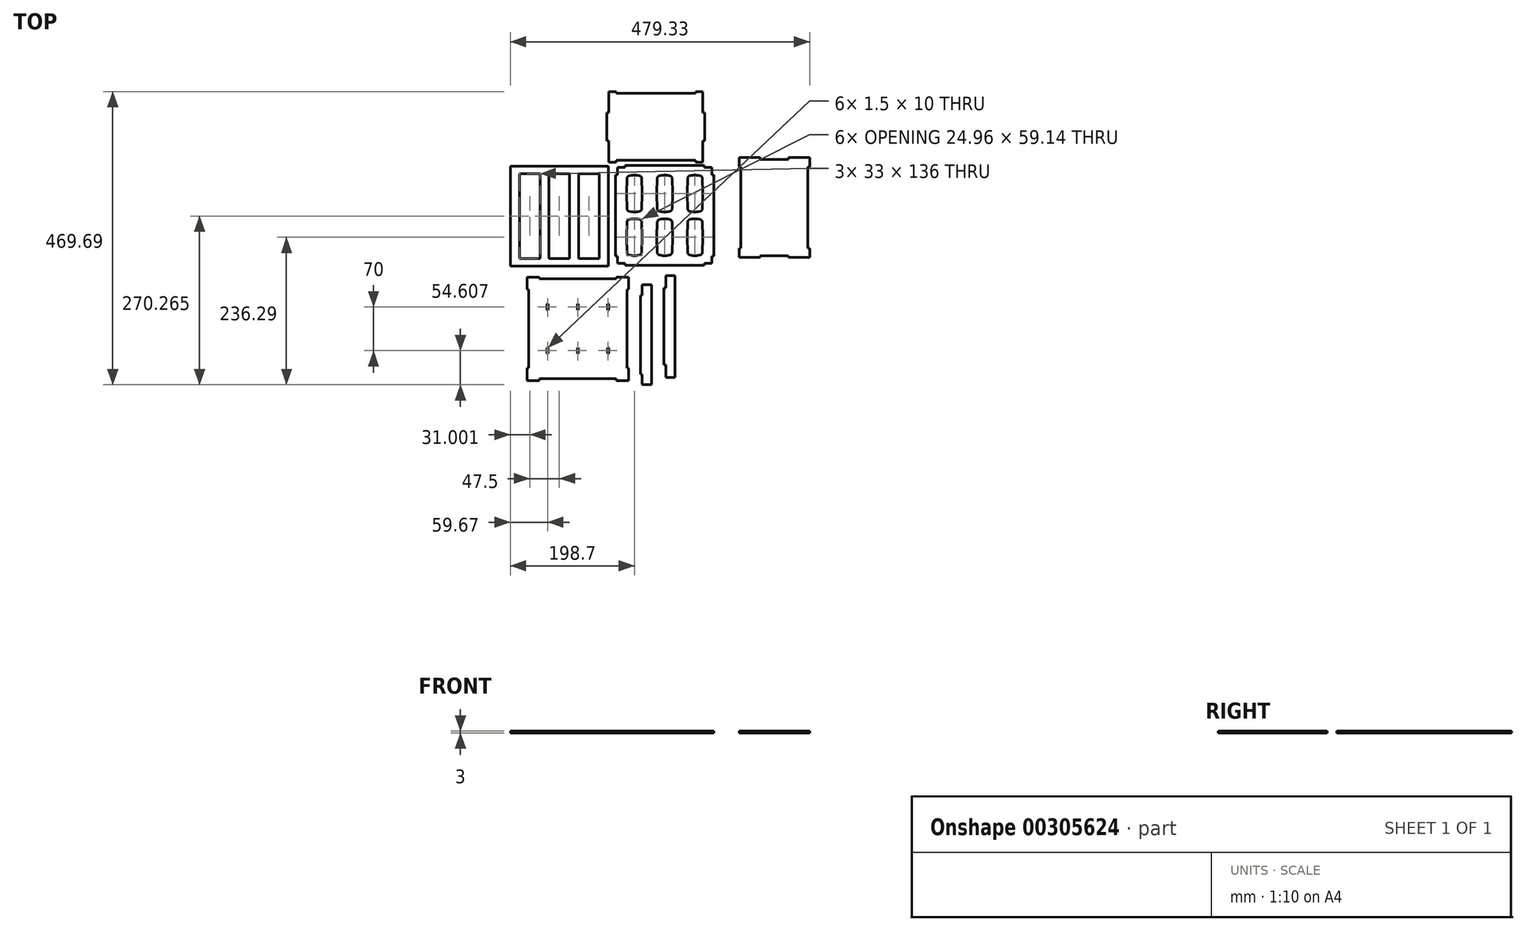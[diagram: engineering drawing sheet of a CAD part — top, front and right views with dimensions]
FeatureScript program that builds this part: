
annotation { "Feature Type Name" : "Feature", "Feature Type Description" : "" }
export const myFeature = defineFeature(function(context is Context, id is Id, definition is map)
    precondition{}
    {
        {
            var Q0;
            Q0=qCreatedBy(makeId("Top.planeOp"),FACE);
            var sketch = newSketch(context, id + "F0", { "sketchPlane" : qUnion([Q0])});
            skLineSegment(sketch, "E0.bottom", {"start": v(12.5, -30) * mm, "end": v(-12.5, -30) * mm, "construction": true});
            skLineSegment(sketch, "E0.top", {"start": v(12.5, 30) * mm, "end": v(-12.5, 30) * mm, "construction": true});
            skLineSegment(sketch, "E0.left", {"start": v(12.5, -30) * mm, "end": v(12.5, 30) * mm, "construction": true});
            skLineSegment(sketch, "E0.right", {"start": v(-12.5, -30) * mm, "end": v(-12.5, 30) * mm, "construction": true});
            skPoint(sketch, "E0.middle", {"position": v(0, 0) * mm});
            skLineSegment(sketch, "E1", {"start": v(-5.03, 29.14) * mm, "end": v(-7.7, 28.69) * mm});
            skLineSegment(sketch, "E2", {"start": v(-11.86, 23.9) * mm, "end": v(-12.46, 1.34) * mm});
            skLineSegment(sketch, "E3", {"start": v(5.03, 29.14) * mm, "end": v(7.7, 28.69) * mm});
            skLineSegment(sketch, "E4", {"start": v(11.86, 23.9) * mm, "end": v(12.46, 1.34) * mm});
            skLineSegment(sketch, "E5", {"start": v(12.46, -1.34) * mm, "end": v(11.86, -23.9) * mm});
            skLineSegment(sketch, "E6", {"start": v(7.7, -28.69) * mm, "end": v(5.03, -29.14) * mm});
            skLineSegment(sketch, "E7", {"start": v(-5.03, -29.14) * mm, "end": v(-7.7, -28.69) * mm});
            skLineSegment(sketch, "E8", {"start": v(-11.86, -23.9) * mm, "end": v(-12.46, -1.34) * mm});
            skPoint(sketch, "E9.visualSharp", {"position": v(-11.75, 28) * mm});
            skArc(sketch, "E9.filletArc", {"start": v(-7.7, 28.69) * mm, "mid": v(-10.64, 27.04) * mm, "end": v(-11.86, 23.9) * mm});
            skPoint(sketch, "E10.visualSharp", {"position": v(11.75, 28) * mm});
            skArc(sketch, "E10.filletArc", {"start": v(11.86, 23.9) * mm, "mid": v(10.64, 27.04) * mm, "end": v(7.7, 28.69) * mm});
            skPoint(sketch, "E11.visualSharp", {"position": v(11.75, -28) * mm});
            skArc(sketch, "E11.filletArc", {"start": v(7.7, -28.69) * mm, "mid": v(10.64, -27.04) * mm, "end": v(11.86, -23.9) * mm});
            skPoint(sketch, "E12.visualSharp", {"position": v(-11.75, -28) * mm});
            skArc(sketch, "E12.filletArc", {"start": v(-11.86, -23.9) * mm, "mid": v(-10.64, -27.04) * mm, "end": v(-7.7, -28.69) * mm});
            skPoint(sketch, "E13.visualSharp", {"position": v(0, -30) * mm});
            skArc(sketch, "E13.filletArc", {"start": v(-5.03, -29.14) * mm, "mid": v(0, -29.57) * mm, "end": v(5.03, -29.14) * mm});
            skPoint(sketch, "E14.visualSharp", {"position": v(0, 30) * mm});
            skArc(sketch, "E14.filletArc", {"start": v(5.03, 29.14) * mm, "mid": v(0, 29.57) * mm, "end": v(-5.03, 29.14) * mm});
            skPoint(sketch, "E15.visualSharp", {"position": v(-12.5, 0) * mm});
            skArc(sketch, "E15.filletArc", {"start": v(-12.46, 1.34) * mm, "mid": v(-12.48, 0) * mm, "end": v(-12.46, -1.34) * mm});
            skPoint(sketch, "E16.visualSharp", {"position": v(12.5, 0) * mm});
            skArc(sketch, "E16.filletArc", {"start": v(12.46, -1.34) * mm, "mid": v(12.48, 0) * mm, "end": v(12.46, 1.34) * mm});
            skPoint(sketch, "E17.0.1.0", {"position": v(0, 100) * mm});
            skLineSegment(sketch, "E17.0.1.1", {"start": v(12.46, 68.66) * mm, "end": v(11.86, 46.1) * mm});
            skLineSegment(sketch, "E17.0.1.2", {"start": v(11.86, 93.9) * mm, "end": v(12.46, 71.34) * mm});
            skLineSegment(sketch, "E17.0.1.3", {"start": v(-12.5, 40) * mm, "end": v(-12.5, 100) * mm, "construction": true});
            skLineSegment(sketch, "E17.0.1.4", {"start": v(12.5, 40) * mm, "end": v(12.5, 100) * mm, "construction": true});
            skPoint(sketch, "E17.0.1.5", {"position": v(-12.5, 70) * mm});
            skPoint(sketch, "E17.0.1.6", {"position": v(12.5, 70) * mm});
            skPoint(sketch, "E17.0.1.7", {"position": v(-11.75, 98) * mm});
            skPoint(sketch, "E17.0.1.8", {"position": v(11.75, 42) * mm});
            skPoint(sketch, "E17.0.1.9", {"position": v(-11.75, 42) * mm});
            skPoint(sketch, "E17.0.1.10", {"position": v(0, 40) * mm});
            skPoint(sketch, "E17.0.1.11", {"position": v(11.75, 98) * mm});
            skArc(sketch, "E17.0.1.12", {"start": v(5.03, 99.14) * mm, "mid": v(0, 99.57) * mm, "end": v(-5.03, 99.14) * mm});
            skArc(sketch, "E17.0.1.13", {"start": v(-5.03, 40.86) * mm, "mid": v(0, 40.43) * mm, "end": v(5.03, 40.86) * mm});
            skLineSegment(sketch, "E17.0.1.14", {"start": v(-11.86, 46.1) * mm, "end": v(-12.46, 68.66) * mm});
            skPoint(sketch, "E17.0.1.15", {"position": v(0, 70) * mm});
            skLineSegment(sketch, "E17.0.1.16", {"start": v(-11.86, 93.9) * mm, "end": v(-12.46, 71.34) * mm});
            skLineSegment(sketch, "E17.0.1.17", {"start": v(12.5, 100) * mm, "end": v(-12.5, 100) * mm, "construction": true});
            skLineSegment(sketch, "E17.0.1.18", {"start": v(12.5, 40) * mm, "end": v(-12.5, 40) * mm, "construction": true});
            skLineSegment(sketch, "E17.0.1.19", {"start": v(-5.03, 40.86) * mm, "end": v(-7.7, 41.31) * mm});
            skLineSegment(sketch, "E17.0.1.20", {"start": v(7.7, 41.31) * mm, "end": v(5.03, 40.86) * mm});
            skArc(sketch, "E17.0.1.21", {"start": v(-11.86, 46.1) * mm, "mid": v(-10.64, 42.96) * mm, "end": v(-7.7, 41.31) * mm});
            skArc(sketch, "E17.0.1.22", {"start": v(7.7, 41.31) * mm, "mid": v(10.64, 42.96) * mm, "end": v(11.86, 46.1) * mm});
            skArc(sketch, "E17.0.1.23", {"start": v(11.86, 93.9) * mm, "mid": v(10.64, 97.04) * mm, "end": v(7.7, 98.69) * mm});
            skArc(sketch, "E17.0.1.24", {"start": v(-7.7, 98.69) * mm, "mid": v(-10.64, 97.04) * mm, "end": v(-11.86, 93.9) * mm});
            skLineSegment(sketch, "E17.0.1.25", {"start": v(5.03, 99.14) * mm, "end": v(7.7, 98.69) * mm});
            skLineSegment(sketch, "E17.0.1.26", {"start": v(-5.03, 99.14) * mm, "end": v(-7.7, 98.69) * mm});
            skArc(sketch, "E17.0.1.27", {"start": v(-12.46, 71.34) * mm, "mid": v(-12.48, 70) * mm, "end": v(-12.46, 68.66) * mm});
            skArc(sketch, "E17.0.1.28", {"start": v(12.46, 68.66) * mm, "mid": v(12.48, 70) * mm, "end": v(12.46, 71.34) * mm});
            skPoint(sketch, "E17.1.0.0", {"position": v(48.5, 30) * mm});
            skLineSegment(sketch, "E17.1.0.1", {"start": v(60.96, -1.34) * mm, "end": v(60.36, -23.9) * mm});
            skLineSegment(sketch, "E17.1.0.2", {"start": v(60.36, 23.9) * mm, "end": v(60.96, 1.34) * mm});
            skLineSegment(sketch, "E17.1.0.3", {"start": v(36, -30) * mm, "end": v(36, 30) * mm, "construction": true});
            skLineSegment(sketch, "E17.1.0.4", {"start": v(61, -30) * mm, "end": v(61, 30) * mm, "construction": true});
            skPoint(sketch, "E17.1.0.5", {"position": v(36, 0) * mm});
            skPoint(sketch, "E17.1.0.6", {"position": v(61, 0) * mm});
            skPoint(sketch, "E17.1.0.7", {"position": v(36.75, 28) * mm});
            skPoint(sketch, "E17.1.0.8", {"position": v(60.25, -28) * mm});
            skPoint(sketch, "E17.1.0.9", {"position": v(36.75, -28) * mm});
            skPoint(sketch, "E17.1.0.10", {"position": v(48.5, -30) * mm});
            skPoint(sketch, "E17.1.0.11", {"position": v(60.25, 28) * mm});
            skArc(sketch, "E17.1.0.12", {"start": v(53.53, 29.14) * mm, "mid": v(48.5, 29.57) * mm, "end": v(43.47, 29.14) * mm});
            skArc(sketch, "E17.1.0.13", {"start": v(43.47, -29.14) * mm, "mid": v(48.5, -29.57) * mm, "end": v(53.53, -29.14) * mm});
            skLineSegment(sketch, "E17.1.0.14", {"start": v(36.64, -23.9) * mm, "end": v(36.04, -1.34) * mm});
            skPoint(sketch, "E17.1.0.15", {"position": v(48.5, 0) * mm});
            skLineSegment(sketch, "E17.1.0.16", {"start": v(36.64, 23.9) * mm, "end": v(36.04, 1.34) * mm});
            skLineSegment(sketch, "E17.1.0.17", {"start": v(61, 30) * mm, "end": v(36, 30) * mm, "construction": true});
            skLineSegment(sketch, "E17.1.0.18", {"start": v(61, -30) * mm, "end": v(36, -30) * mm, "construction": true});
            skLineSegment(sketch, "E17.1.0.19", {"start": v(43.47, -29.14) * mm, "end": v(40.8, -28.69) * mm});
            skLineSegment(sketch, "E17.1.0.20", {"start": v(56.2, -28.69) * mm, "end": v(53.53, -29.14) * mm});
            skArc(sketch, "E17.1.0.21", {"start": v(36.64, -23.9) * mm, "mid": v(37.86, -27.04) * mm, "end": v(40.8, -28.69) * mm});
            skArc(sketch, "E17.1.0.22", {"start": v(56.2, -28.69) * mm, "mid": v(59.14, -27.04) * mm, "end": v(60.36, -23.9) * mm});
            skArc(sketch, "E17.1.0.23", {"start": v(60.36, 23.9) * mm, "mid": v(59.14, 27.04) * mm, "end": v(56.2, 28.69) * mm});
            skArc(sketch, "E17.1.0.24", {"start": v(40.8, 28.69) * mm, "mid": v(37.86, 27.04) * mm, "end": v(36.64, 23.9) * mm});
            skLineSegment(sketch, "E17.1.0.25", {"start": v(53.53, 29.14) * mm, "end": v(56.2, 28.69) * mm});
            skLineSegment(sketch, "E17.1.0.26", {"start": v(43.47, 29.14) * mm, "end": v(40.8, 28.69) * mm});
            skArc(sketch, "E17.1.0.27", {"start": v(36.04, 1.34) * mm, "mid": v(36.02, 0) * mm, "end": v(36.04, -1.34) * mm});
            skArc(sketch, "E17.1.0.28", {"start": v(60.96, -1.34) * mm, "mid": v(60.98, 0) * mm, "end": v(60.96, 1.34) * mm});
            skPoint(sketch, "E17.1.1.0", {"position": v(48.5, 100) * mm});
            skLineSegment(sketch, "E17.1.1.1", {"start": v(60.96, 68.66) * mm, "end": v(60.36, 46.1) * mm});
            skLineSegment(sketch, "E17.1.1.2", {"start": v(60.36, 93.9) * mm, "end": v(60.96, 71.34) * mm});
            skLineSegment(sketch, "E17.1.1.3", {"start": v(36, 40) * mm, "end": v(36, 100) * mm, "construction": true});
            skLineSegment(sketch, "E17.1.1.4", {"start": v(61, 40) * mm, "end": v(61, 100) * mm, "construction": true});
            skPoint(sketch, "E17.1.1.5", {"position": v(36, 70) * mm});
            skPoint(sketch, "E17.1.1.6", {"position": v(61, 70) * mm});
            skPoint(sketch, "E17.1.1.7", {"position": v(36.75, 98) * mm});
            skPoint(sketch, "E17.1.1.8", {"position": v(60.25, 42) * mm});
            skPoint(sketch, "E17.1.1.9", {"position": v(36.75, 42) * mm});
            skPoint(sketch, "E17.1.1.10", {"position": v(48.5, 40) * mm});
            skPoint(sketch, "E17.1.1.11", {"position": v(60.25, 98) * mm});
            skArc(sketch, "E17.1.1.12", {"start": v(53.53, 99.14) * mm, "mid": v(48.5, 99.57) * mm, "end": v(43.47, 99.14) * mm});
            skArc(sketch, "E17.1.1.13", {"start": v(43.47, 40.86) * mm, "mid": v(48.5, 40.43) * mm, "end": v(53.53, 40.86) * mm});
            skLineSegment(sketch, "E17.1.1.14", {"start": v(36.64, 46.1) * mm, "end": v(36.04, 68.66) * mm});
            skPoint(sketch, "E17.1.1.15", {"position": v(48.5, 70) * mm});
            skLineSegment(sketch, "E17.1.1.16", {"start": v(36.64, 93.9) * mm, "end": v(36.04, 71.34) * mm});
            skLineSegment(sketch, "E17.1.1.17", {"start": v(61, 100) * mm, "end": v(36, 100) * mm, "construction": true});
            skLineSegment(sketch, "E17.1.1.18", {"start": v(61, 40) * mm, "end": v(36, 40) * mm, "construction": true});
            skLineSegment(sketch, "E17.1.1.19", {"start": v(43.47, 40.86) * mm, "end": v(40.8, 41.31) * mm});
            skLineSegment(sketch, "E17.1.1.20", {"start": v(56.2, 41.31) * mm, "end": v(53.53, 40.86) * mm});
            skArc(sketch, "E17.1.1.21", {"start": v(36.64, 46.1) * mm, "mid": v(37.86, 42.96) * mm, "end": v(40.8, 41.31) * mm});
            skArc(sketch, "E17.1.1.22", {"start": v(56.2, 41.31) * mm, "mid": v(59.14, 42.96) * mm, "end": v(60.36, 46.1) * mm});
            skArc(sketch, "E17.1.1.23", {"start": v(60.36, 93.9) * mm, "mid": v(59.14, 97.04) * mm, "end": v(56.2, 98.69) * mm});
            skArc(sketch, "E17.1.1.24", {"start": v(40.8, 98.69) * mm, "mid": v(37.86, 97.04) * mm, "end": v(36.64, 93.9) * mm});
            skLineSegment(sketch, "E17.1.1.25", {"start": v(53.53, 99.14) * mm, "end": v(56.2, 98.69) * mm});
            skLineSegment(sketch, "E17.1.1.26", {"start": v(43.47, 99.14) * mm, "end": v(40.8, 98.69) * mm});
            skArc(sketch, "E17.1.1.27", {"start": v(36.04, 71.34) * mm, "mid": v(36.02, 70) * mm, "end": v(36.04, 68.66) * mm});
            skArc(sketch, "E17.1.1.28", {"start": v(60.96, 68.66) * mm, "mid": v(60.98, 70) * mm, "end": v(60.96, 71.34) * mm});
            skPoint(sketch, "E17.2.0.0", {"position": v(97, 30) * mm});
            skLineSegment(sketch, "E17.2.0.1", {"start": v(109.46, -1.34) * mm, "end": v(108.86, -23.9) * mm});
            skLineSegment(sketch, "E17.2.0.2", {"start": v(108.86, 23.9) * mm, "end": v(109.46, 1.34) * mm});
            skLineSegment(sketch, "E17.2.0.3", {"start": v(84.5, -30) * mm, "end": v(84.5, 30) * mm, "construction": true});
            skLineSegment(sketch, "E17.2.0.4", {"start": v(109.5, -30) * mm, "end": v(109.5, 30) * mm, "construction": true});
            skPoint(sketch, "E17.2.0.5", {"position": v(84.5, 0) * mm});
            skPoint(sketch, "E17.2.0.6", {"position": v(109.5, 0) * mm});
            skPoint(sketch, "E17.2.0.7", {"position": v(85.25, 28) * mm});
            skPoint(sketch, "E17.2.0.8", {"position": v(108.75, -28) * mm});
            skPoint(sketch, "E17.2.0.9", {"position": v(85.25, -28) * mm});
            skPoint(sketch, "E17.2.0.10", {"position": v(97, -30) * mm});
            skPoint(sketch, "E17.2.0.11", {"position": v(108.75, 28) * mm});
            skArc(sketch, "E17.2.0.12", {"start": v(102.03, 29.14) * mm, "mid": v(97, 29.57) * mm, "end": v(91.97, 29.14) * mm});
            skArc(sketch, "E17.2.0.13", {"start": v(91.97, -29.14) * mm, "mid": v(97, -29.57) * mm, "end": v(102.03, -29.14) * mm});
            skLineSegment(sketch, "E17.2.0.14", {"start": v(85.14, -23.9) * mm, "end": v(84.54, -1.34) * mm});
            skPoint(sketch, "E17.2.0.15", {"position": v(97, 0) * mm});
            skLineSegment(sketch, "E17.2.0.16", {"start": v(85.14, 23.9) * mm, "end": v(84.54, 1.34) * mm});
            skLineSegment(sketch, "E17.2.0.17", {"start": v(109.5, 30) * mm, "end": v(84.5, 30) * mm, "construction": true});
            skLineSegment(sketch, "E17.2.0.18", {"start": v(109.5, -30) * mm, "end": v(84.5, -30) * mm, "construction": true});
            skLineSegment(sketch, "E17.2.0.19", {"start": v(91.97, -29.14) * mm, "end": v(89.3, -28.69) * mm});
            skLineSegment(sketch, "E17.2.0.20", {"start": v(104.7, -28.69) * mm, "end": v(102.03, -29.14) * mm});
            skArc(sketch, "E17.2.0.21", {"start": v(85.14, -23.9) * mm, "mid": v(86.36, -27.04) * mm, "end": v(89.3, -28.69) * mm});
            skArc(sketch, "E17.2.0.22", {"start": v(104.7, -28.69) * mm, "mid": v(107.64, -27.04) * mm, "end": v(108.86, -23.9) * mm});
            skArc(sketch, "E17.2.0.23", {"start": v(108.86, 23.9) * mm, "mid": v(107.64, 27.04) * mm, "end": v(104.7, 28.69) * mm});
            skArc(sketch, "E17.2.0.24", {"start": v(89.3, 28.69) * mm, "mid": v(86.36, 27.04) * mm, "end": v(85.14, 23.9) * mm});
            skLineSegment(sketch, "E17.2.0.25", {"start": v(102.03, 29.14) * mm, "end": v(104.7, 28.69) * mm});
            skLineSegment(sketch, "E17.2.0.26", {"start": v(91.97, 29.14) * mm, "end": v(89.3, 28.69) * mm});
            skArc(sketch, "E17.2.0.27", {"start": v(84.54, 1.34) * mm, "mid": v(84.52, 0) * mm, "end": v(84.54, -1.34) * mm});
            skArc(sketch, "E17.2.0.28", {"start": v(109.46, -1.34) * mm, "mid": v(109.48, 0) * mm, "end": v(109.46, 1.34) * mm});
            skPoint(sketch, "E17.2.1.0", {"position": v(97, 100) * mm});
            skLineSegment(sketch, "E17.2.1.1", {"start": v(109.46, 68.66) * mm, "end": v(108.86, 46.1) * mm});
            skLineSegment(sketch, "E17.2.1.2", {"start": v(108.86, 93.9) * mm, "end": v(109.46, 71.34) * mm});
            skLineSegment(sketch, "E17.2.1.3", {"start": v(84.5, 40) * mm, "end": v(84.5, 100) * mm, "construction": true});
            skLineSegment(sketch, "E17.2.1.4", {"start": v(109.5, 40) * mm, "end": v(109.5, 100) * mm, "construction": true});
            skPoint(sketch, "E17.2.1.5", {"position": v(84.5, 70) * mm});
            skPoint(sketch, "E17.2.1.6", {"position": v(109.5, 70) * mm});
            skPoint(sketch, "E17.2.1.7", {"position": v(85.25, 98) * mm});
            skPoint(sketch, "E17.2.1.8", {"position": v(108.75, 42) * mm});
            skPoint(sketch, "E17.2.1.9", {"position": v(85.25, 42) * mm});
            skPoint(sketch, "E17.2.1.10", {"position": v(97, 40) * mm});
            skPoint(sketch, "E17.2.1.11", {"position": v(108.75, 98) * mm});
            skArc(sketch, "E17.2.1.12", {"start": v(102.03, 99.14) * mm, "mid": v(97, 99.57) * mm, "end": v(91.97, 99.14) * mm});
            skArc(sketch, "E17.2.1.13", {"start": v(91.97, 40.86) * mm, "mid": v(97, 40.43) * mm, "end": v(102.03, 40.86) * mm});
            skLineSegment(sketch, "E17.2.1.14", {"start": v(85.14, 46.1) * mm, "end": v(84.54, 68.66) * mm});
            skPoint(sketch, "E17.2.1.15", {"position": v(97, 70) * mm});
            skLineSegment(sketch, "E17.2.1.16", {"start": v(85.14, 93.9) * mm, "end": v(84.54, 71.34) * mm});
            skLineSegment(sketch, "E17.2.1.17", {"start": v(109.5, 100) * mm, "end": v(84.5, 100) * mm, "construction": true});
            skLineSegment(sketch, "E17.2.1.18", {"start": v(109.5, 40) * mm, "end": v(84.5, 40) * mm, "construction": true});
            skLineSegment(sketch, "E17.2.1.19", {"start": v(91.97, 40.86) * mm, "end": v(89.3, 41.31) * mm});
            skLineSegment(sketch, "E17.2.1.20", {"start": v(104.7, 41.31) * mm, "end": v(102.03, 40.86) * mm});
            skArc(sketch, "E17.2.1.21", {"start": v(85.14, 46.1) * mm, "mid": v(86.36, 42.96) * mm, "end": v(89.3, 41.31) * mm});
            skArc(sketch, "E17.2.1.22", {"start": v(104.7, 41.31) * mm, "mid": v(107.64, 42.96) * mm, "end": v(108.86, 46.1) * mm});
            skArc(sketch, "E17.2.1.23", {"start": v(108.86, 93.9) * mm, "mid": v(107.64, 97.04) * mm, "end": v(104.7, 98.69) * mm});
            skArc(sketch, "E17.2.1.24", {"start": v(89.3, 98.69) * mm, "mid": v(86.36, 97.04) * mm, "end": v(85.14, 93.9) * mm});
            skLineSegment(sketch, "E17.2.1.25", {"start": v(102.03, 99.14) * mm, "end": v(104.7, 98.69) * mm});
            skLineSegment(sketch, "E17.2.1.26", {"start": v(91.97, 99.14) * mm, "end": v(89.3, 98.69) * mm});
            skArc(sketch, "E17.2.1.27", {"start": v(84.54, 71.34) * mm, "mid": v(84.52, 70) * mm, "end": v(84.54, 68.66) * mm});
            skArc(sketch, "E17.2.1.28", {"start": v(109.46, 68.66) * mm, "mid": v(109.48, 70) * mm, "end": v(109.46, 71.34) * mm});
            skLineSegment(sketch, "E17.direction1", {"start": v(-12.5, -30) * mm, "end": v(36, -30) * mm, "construction": true});
            skLineSegment(sketch, "E17.direction2", {"start": v(-12.5, -30) * mm, "end": v(-12.5, 40) * mm, "construction": true});
            skPoint(sketch, "E18.visualSharp", {"position": v(-30, 115) * mm});
            skPoint(sketch, "E19.visualSharp", {"position": v(127, 115) * mm});
            skPoint(sketch, "E20.visualSharp", {"position": v(-30, -45) * mm});
            skLineSegment(sketch, "E21.bottom", {"start": v(-15, 115) * mm, "end": v(112, 115) * mm});
            skLineSegment(sketch, "E21.top", {"start": v(-15, -45) * mm, "end": v(112, -45) * mm});
            skLineSegment(sketch, "E21.left", {"start": v(-30, 100) * mm, "end": v(-30, -30) * mm});
            skLineSegment(sketch, "E22", {"start": v(-30, 100) * mm, "end": v(-27, 100) * mm});
            skLineSegment(sketch, "E23", {"start": v(-27, 100) * mm, "end": v(-27, 112) * mm});
            skLineSegment(sketch, "E24", {"start": v(-27, 112) * mm, "end": v(-15, 112) * mm});
            skLineSegment(sketch, "E25", {"start": v(-15, 112) * mm, "end": v(-15, 115) * mm});
            skLineSegment(sketch, "E26", {"start": v(-30, -30) * mm, "end": v(-27, -30) * mm});
            skLineSegment(sketch, "E27", {"start": v(-27, -30) * mm, "end": v(-27, -42) * mm});
            skLineSegment(sketch, "E28", {"start": v(-27, -42) * mm, "end": v(-15, -42) * mm});
            skLineSegment(sketch, "E29", {"start": v(-15, -42) * mm, "end": v(-15, -45) * mm});
            skLineSegment(sketch, "E30", {"start": v(127, -30) * mm, "end": v(124, -30) * mm});
            skLineSegment(sketch, "E31", {"start": v(124, -30) * mm, "end": v(124, -42) * mm});
            skLineSegment(sketch, "E32", {"start": v(124, -42) * mm, "end": v(112, -42) * mm});
            skLineSegment(sketch, "E33", {"start": v(112, -42) * mm, "end": v(112, -45) * mm});
            skLineSegment(sketch, "E34", {"start": v(112, 115) * mm, "end": v(112, 112) * mm});
            skLineSegment(sketch, "E35", {"start": v(112, 112) * mm, "end": v(124, 112) * mm});
            skLineSegment(sketch, "E36", {"start": v(124, 112) * mm, "end": v(124, 100) * mm});
            skLineSegment(sketch, "E37", {"start": v(124, 100) * mm, "end": v(127, 100) * mm});
            skLineSegment(sketch, "E38", {"start": v(127, 100) * mm, "end": v(127, -30) * mm});
            skSolve(sketch);
        }
        {
            var Q0;
            Q0 = qSketchRegion(id + "F0", true);
            extrude(context, id + "F1", {"entities" : qUnion([Q0]), "depth" : 3 * mm});
        }
        {
            var Q0;
            Q0=qCreatedBy(makeId("Top.planeOp"),FACE);
            var sketch = newSketch(context, id + "F2", { "sketchPlane" : qUnion([Q0])});
            skPoint(sketch, "E39.visualSharp", {"position": v(-41.7, 113.97) * mm});
            skPoint(sketch, "E40.visualSharp", {"position": v(-41.7, -46.03) * mm});
            skPoint(sketch, "E41.visualSharp", {"position": v(-198.7, -46.03) * mm});
            skPoint(sketch, "E42.visualSharp", {"position": v(-198.7, 113.97) * mm});
            skLineSegment(sketch, "E43.bottom", {"start": v(-184.2, 101.97) * mm, "end": v(-151.2, 101.97) * mm});
            skLineSegment(sketch, "E43.top", {"start": v(-184.2, -34.03) * mm, "end": v(-151.2, -34.03) * mm});
            skLineSegment(sketch, "E43.left", {"start": v(-184.2, 101.97) * mm, "end": v(-184.2, -34.03) * mm});
            skLineSegment(sketch, "E43.right", {"start": v(-151.2, 101.97) * mm, "end": v(-151.2, -34.03) * mm});
            skLineSegment(sketch, "E44.bottom", {"start": v(-136.7, 101.97) * mm, "end": v(-103.7, 101.97) * mm});
            skLineSegment(sketch, "E44.top", {"start": v(-136.7, -34.03) * mm, "end": v(-103.7, -34.03) * mm});
            skLineSegment(sketch, "E44.left", {"start": v(-136.7, 101.97) * mm, "end": v(-136.7, -34.03) * mm});
            skLineSegment(sketch, "E44.right", {"start": v(-103.7, 101.97) * mm, "end": v(-103.7, -34.03) * mm});
            skLineSegment(sketch, "E45.bottom", {"start": v(-89.2, 101.97) * mm, "end": v(-56.2, 101.97) * mm});
            skLineSegment(sketch, "E45.top", {"start": v(-89.2, -34.03) * mm, "end": v(-56.2, -34.03) * mm});
            skLineSegment(sketch, "E45.left", {"start": v(-89.2, 101.97) * mm, "end": v(-89.2, -34.03) * mm});
            skLineSegment(sketch, "E45.right", {"start": v(-56.2, 101.97) * mm, "end": v(-56.2, -34.03) * mm});
            skLineSegment(sketch, "E46.bottom", {"start": v(-198.7, 113.97) * mm, "end": v(-41.7, 113.97) * mm});
            skLineSegment(sketch, "E46.top", {"start": v(-198.7, -46.03) * mm, "end": v(-41.7, -46.03) * mm});
            skLineSegment(sketch, "E46.left", {"start": v(-198.7, 113.97) * mm, "end": v(-198.7, -46.03) * mm});
            skLineSegment(sketch, "E46.right", {"start": v(-41.7, 113.97) * mm, "end": v(-41.7, -46.03) * mm});
            skSolve(sketch);
        }
        {
            var Q0;
            Q0 = qSketchRegion(id + "F2", true);
            extrude(context, id + "F3", {"entities" : qUnion([Q0]), "depth" : 3 * mm});
        }
        {
            var Q0;
            Q0=qCreatedBy(makeId("Top.planeOp"),FACE);
            var sketch = newSketch(context, id + "F4", { "sketchPlane" : qUnion([Q0])});
            skPoint(sketch, "E47.visualSharp", {"position": v(-5.49, -66.68) * mm});
            skPoint(sketch, "E48.visualSharp", {"position": v(-12.03, -226.68) * mm});
            skPoint(sketch, "E49.visualSharp", {"position": v(-169.03, -226.68) * mm});
            skPoint(sketch, "E50.visualSharp", {"position": v(-169.03, -66.68) * mm});
            skLineSegment(sketch, "E51.bottom", {"start": v(-138.28, -116.68) * mm, "end": v(-139.78, -116.68) * mm});
            skLineSegment(sketch, "E51.top", {"start": v(-138.28, -106.68) * mm, "end": v(-139.78, -106.68) * mm});
            skLineSegment(sketch, "E51.left", {"start": v(-138.28, -116.68) * mm, "end": v(-138.28, -106.68) * mm});
            skLineSegment(sketch, "E51.right", {"start": v(-139.78, -116.68) * mm, "end": v(-139.78, -106.68) * mm});
            skPoint(sketch, "E51.middle", {"position": v(-139.03, -111.68) * mm});
            skLineSegment(sketch, "E52.0.1.0", {"start": v(-139.78, -186.68) * mm, "end": v(-139.78, -176.68) * mm});
            skLineSegment(sketch, "E52.0.1.1", {"start": v(-138.28, -186.68) * mm, "end": v(-138.28, -176.68) * mm});
            skPoint(sketch, "E52.0.1.2", {"position": v(-139.03, -181.68) * mm});
            skLineSegment(sketch, "E52.0.1.3", {"start": v(-138.28, -176.68) * mm, "end": v(-139.78, -176.68) * mm});
            skLineSegment(sketch, "E52.0.1.4", {"start": v(-138.28, -186.68) * mm, "end": v(-139.78, -186.68) * mm});
            skLineSegment(sketch, "E52.1.0.0", {"start": v(-91.28, -116.68) * mm, "end": v(-91.28, -106.68) * mm});
            skLineSegment(sketch, "E52.1.0.1", {"start": v(-89.78, -116.68) * mm, "end": v(-89.78, -106.68) * mm});
            skPoint(sketch, "E52.1.0.2", {"position": v(-90.53, -111.68) * mm});
            skLineSegment(sketch, "E52.1.0.3", {"start": v(-89.78, -106.68) * mm, "end": v(-91.28, -106.68) * mm});
            skLineSegment(sketch, "E52.1.0.4", {"start": v(-89.78, -116.68) * mm, "end": v(-91.28, -116.68) * mm});
            skLineSegment(sketch, "E52.1.1.0", {"start": v(-91.28, -186.68) * mm, "end": v(-91.28, -176.68) * mm});
            skLineSegment(sketch, "E52.1.1.1", {"start": v(-89.78, -186.68) * mm, "end": v(-89.78, -176.68) * mm});
            skPoint(sketch, "E52.1.1.2", {"position": v(-90.53, -181.68) * mm});
            skLineSegment(sketch, "E52.1.1.3", {"start": v(-89.78, -176.68) * mm, "end": v(-91.28, -176.68) * mm});
            skLineSegment(sketch, "E52.1.1.4", {"start": v(-89.78, -186.68) * mm, "end": v(-91.28, -186.68) * mm});
            skLineSegment(sketch, "E52.2.0.0", {"start": v(-42.78, -116.68) * mm, "end": v(-42.78, -106.68) * mm});
            skLineSegment(sketch, "E52.2.0.1", {"start": v(-41.28, -116.68) * mm, "end": v(-41.28, -106.68) * mm});
            skPoint(sketch, "E52.2.0.2", {"position": v(-42.03, -111.68) * mm});
            skLineSegment(sketch, "E52.2.0.3", {"start": v(-41.28, -106.68) * mm, "end": v(-42.78, -106.68) * mm});
            skLineSegment(sketch, "E52.2.0.4", {"start": v(-41.28, -116.68) * mm, "end": v(-42.78, -116.68) * mm});
            skLineSegment(sketch, "E52.2.1.0", {"start": v(-42.78, -186.68) * mm, "end": v(-42.78, -176.68) * mm});
            skLineSegment(sketch, "E52.2.1.1", {"start": v(-41.28, -186.68) * mm, "end": v(-41.28, -176.68) * mm});
            skPoint(sketch, "E52.2.1.2", {"position": v(-42.03, -181.68) * mm});
            skLineSegment(sketch, "E52.2.1.3", {"start": v(-41.28, -176.68) * mm, "end": v(-42.78, -176.68) * mm});
            skLineSegment(sketch, "E52.2.1.4", {"start": v(-41.28, -186.68) * mm, "end": v(-42.78, -186.68) * mm});
            skLineSegment(sketch, "E52.direction1", {"start": v(-139.03, -111.68) * mm, "end": v(-90.53, -111.68) * mm, "construction": true});
            skLineSegment(sketch, "E52.direction2", {"start": v(-139.03, -111.68) * mm, "end": v(-139.03, -181.68) * mm, "construction": true});
            skLineSegment(sketch, "E53.bottom", {"start": v(-152.03, -66.68) * mm, "end": v(-29.03, -66.68) * mm});
            skLineSegment(sketch, "E53.top", {"start": v(-152.03, -226.68) * mm, "end": v(-29.03, -226.68) * mm});
            skLineSegment(sketch, "E53.left", {"start": v(-169.03, -83.68) * mm, "end": v(-169.03, -209.68) * mm});
            skLineSegment(sketch, "E53.right", {"start": v(-12.03, -83.68) * mm, "end": v(-12.03, -209.68) * mm});
            skLineSegment(sketch, "E54", {"start": v(-169.03, -83.68) * mm, "end": v(-172.03, -83.68) * mm});
            skLineSegment(sketch, "E55", {"start": v(-172.03, -83.68) * mm, "end": v(-172.03, -63.68) * mm});
            skLineSegment(sketch, "E56", {"start": v(-172.03, -63.68) * mm, "end": v(-152.03, -63.68) * mm});
            skLineSegment(sketch, "E57", {"start": v(-152.03, -63.68) * mm, "end": v(-152.03, -66.68) * mm});
            skLineSegment(sketch, "E58", {"start": v(-169.03, -209.68) * mm, "end": v(-172.03, -209.68) * mm});
            skLineSegment(sketch, "E59", {"start": v(-172.03, -209.68) * mm, "end": v(-172.03, -229.68) * mm});
            skLineSegment(sketch, "E60", {"start": v(-172.03, -229.68) * mm, "end": v(-152.03, -229.68) * mm});
            skLineSegment(sketch, "E61", {"start": v(-152.03, -229.68) * mm, "end": v(-152.03, -226.68) * mm});
            skLineSegment(sketch, "E62", {"start": v(-29.03, -226.68) * mm, "end": v(-29.03, -229.68) * mm});
            skLineSegment(sketch, "E63", {"start": v(-29.03, -229.68) * mm, "end": v(-9.03, -229.68) * mm});
            skLineSegment(sketch, "E64", {"start": v(-9.03, -229.68) * mm, "end": v(-9.03, -209.68) * mm});
            skLineSegment(sketch, "E65", {"start": v(-9.03, -209.68) * mm, "end": v(-12.03, -209.68) * mm});
            skLineSegment(sketch, "E66", {"start": v(-12.03, -83.68) * mm, "end": v(-9.03, -83.68) * mm});
            skLineSegment(sketch, "E67", {"start": v(-9.03, -83.68) * mm, "end": v(-9.03, -63.68) * mm});
            skLineSegment(sketch, "E68", {"start": v(-9.03, -63.68) * mm, "end": v(-29.03, -63.68) * mm});
            skLineSegment(sketch, "E69", {"start": v(-29.03, -63.68) * mm, "end": v(-29.03, -66.68) * mm});
            skSolve(sketch);
        }
        {
            var Q0;
            Q0 = qSketchRegion(id + "F4", true);
            extrude(context, id + "F5", {"entities" : qUnion([Q0]), "depth" : 3 * mm});
        }
        {
            var Q0;
            Q0=qCreatedBy(makeId("Top.planeOp"),FACE);
            var sketch = newSketch(context, id + "F6", { "sketchPlane" : qUnion([Q0])});
            skLineSegment(sketch, "E70.bottom", {"start": v(12.59, -76.29) * mm, "end": v(27.59, -76.29) * mm});
            skLineSegment(sketch, "E70.top", {"start": v(12.59, -236.29) * mm, "end": v(27.59, -236.29) * mm});
            skLineSegment(sketch, "E70.left", {"start": v(9.59, -93.29) * mm, "end": v(9.59, -219.29) * mm});
            skLineSegment(sketch, "E70.right", {"start": v(27.59, -76.29) * mm, "end": v(27.59, -236.29) * mm});
            skLineSegment(sketch, "E71", {"start": v(9.59, -93.29) * mm, "end": v(12.59, -93.29) * mm});
            skLineSegment(sketch, "E72", {"start": v(12.59, -93.29) * mm, "end": v(12.59, -76.29) * mm});
            skLineSegment(sketch, "E73", {"start": v(9.59, -219.29) * mm, "end": v(12.59, -219.29) * mm});
            skLineSegment(sketch, "E74", {"start": v(12.59, -219.29) * mm, "end": v(12.59, -236.29) * mm});
            skSolve(sketch);
        }
        {
            var Q0;
            Q0 = qSketchRegion(id + "F6", true);
            extrude(context, id + "F7", {"entities" : qUnion([Q0]), "depth" : 3 * mm});
        }
        {
            var Q0;
            Q0=qCreatedBy(makeId("Top.planeOp"),FACE);
            var sketch = newSketch(context, id + "F8", { "sketchPlane" : qUnion([Q0])});
            skLineSegment(sketch, "E75.bottom", {"start": v(50.23, -61.3) * mm, "end": v(65.23, -61.3) * mm});
            skLineSegment(sketch, "E75.top", {"start": v(50.23, -224.3) * mm, "end": v(65.23, -224.3) * mm});
            skLineSegment(sketch, "E75.left", {"start": v(47.23, -81.3) * mm, "end": v(47.23, -204.3) * mm});
            skLineSegment(sketch, "E75.right", {"start": v(65.23, -61.3) * mm, "end": v(65.23, -224.3) * mm});
            skLineSegment(sketch, "E76", {"start": v(50.23, -61.3) * mm, "end": v(50.23, -81.3) * mm});
            skLineSegment(sketch, "E77", {"start": v(50.23, -81.3) * mm, "end": v(47.23, -81.3) * mm});
            skLineSegment(sketch, "E78", {"start": v(47.23, -204.3) * mm, "end": v(50.23, -204.3) * mm});
            skLineSegment(sketch, "E79", {"start": v(50.23, -204.3) * mm, "end": v(50.23, -224.3) * mm});
            skSolve(sketch);
        }
        {
            var Q0;
            Q0 = qSketchRegion(id + "F8", true);
            extrude(context, id + "F9", {"entities" : qUnion([Q0]), "depth" : 3 * mm});
        }
        {
            var Q0;
            Q0=qCreatedBy(makeId("Top.planeOp"),FACE);
            var sketch = newSketch(context, id + "F10", { "sketchPlane" : qUnion([Q0])});
            skLineSegment(sketch, "E80.bottom", {"start": v(170.6, 127.5) * mm, "end": v(201.63, 127.5) * mm});
            skLineSegment(sketch, "E80.top", {"start": v(170.6, -32.5) * mm, "end": v(201.63, -32.5) * mm});
            skLineSegment(sketch, "E81", {"start": v(167.63, 112.5) * mm, "end": v(170.63, 112.5) * mm});
            skLineSegment(sketch, "E82", {"start": v(201.63, 127.5) * mm, "end": v(201.63, 124.5) * mm});
            skLineSegment(sketch, "E83", {"start": v(201.63, 124.5) * mm, "end": v(246.63, 124.5) * mm});
            skLineSegment(sketch, "E84", {"start": v(246.63, 124.5) * mm, "end": v(246.63, 127.5) * mm});
            skLineSegment(sketch, "E85", {"start": v(277.63, 112.5) * mm, "end": v(280.63, 112.5) * mm});
            skLineSegment(sketch, "E86", {"start": v(167.63, -17.5) * mm, "end": v(170.63, -17.5) * mm});
            skLineSegment(sketch, "E87", {"start": v(201.63, -32.5) * mm, "end": v(201.63, -29.5) * mm});
            skLineSegment(sketch, "E88", {"start": v(201.63, -29.5) * mm, "end": v(246.63, -29.5) * mm});
            skLineSegment(sketch, "E89", {"start": v(246.63, -29.5) * mm, "end": v(246.63, -32.5) * mm});
            skLineSegment(sketch, "E90", {"start": v(277.63, -17.5) * mm, "end": v(280.63, -17.5) * mm});
            skLineSegment(sketch, "E91.trimOffspring", {"start": v(246.63, -32.5) * mm, "end": v(277.6, -32.5) * mm});
            skLineSegment(sketch, "E92.trimOffspring", {"start": v(246.63, 127.5) * mm, "end": v(277.6, 127.5) * mm});
            skLineSegment(sketch, "E93", {"start": v(170.63, 112.5) * mm, "end": v(170.63, -17.5) * mm});
            skLineSegment(sketch, "E94", {"start": v(277.63, 112.5) * mm, "end": v(277.63, -17.5) * mm});
            skLineSegment(sketch, "E95", {"start": v(167.63, -17.5) * mm, "end": v(167.63, -32.5) * mm});
            skLineSegment(sketch, "E96", {"start": v(167.63, -32.5) * mm, "end": v(170.6, -32.5) * mm});
            skLineSegment(sketch, "E97", {"start": v(280.63, -17.5) * mm, "end": v(280.63, -32.5) * mm});
            skLineSegment(sketch, "E98", {"start": v(280.63, -32.5) * mm, "end": v(277.6, -32.5) * mm});
            skLineSegment(sketch, "E99", {"start": v(280.63, 112.5) * mm, "end": v(280.63, 127.5) * mm});
            skLineSegment(sketch, "E100", {"start": v(280.63, 127.5) * mm, "end": v(277.6, 127.5) * mm});
            skLineSegment(sketch, "E101", {"start": v(167.63, 112.5) * mm, "end": v(167.63, 127.5) * mm});
            skLineSegment(sketch, "E102", {"start": v(167.63, 127.5) * mm, "end": v(170.6, 127.5) * mm});
            skSolve(sketch);
        }
        {
            var Q0;
            Q0 = qSketchRegion(id + "F10", true);
            extrude(context, id + "F11", {"entities" : qUnion([Q0]), "depth" : 3 * mm});
        }
        {
            var Q0;
            Q0=qCreatedBy(makeId("Top.planeOp"),FACE);
            var sketch = newSketch(context, id + "F12", { "sketchPlane" : qUnion([Q0])});
            skLineSegment(sketch, "E103.bottom", {"start": v(-41.26, 120.4) * mm, "end": v(-29.26, 120.4) * mm});
            skLineSegment(sketch, "E103.top", {"start": v(-41.26, 233.4) * mm, "end": v(-29.26, 233.4) * mm});
            skLineSegment(sketch, "E103.left", {"start": v(-44.26, 154.4) * mm, "end": v(-44.26, 199.4) * mm});
            skLineSegment(sketch, "E103.right", {"start": v(112.74, 154.4) * mm, "end": v(112.74, 199.4) * mm});
            skLineSegment(sketch, "E104", {"start": v(-29.26, 123.4) * mm, "end": v(-29.26, 120.4) * mm});
            skLineSegment(sketch, "E105", {"start": v(97.74, 123.14) * mm, "end": v(97.74, 120.4) * mm});
            skLineSegment(sketch, "E106", {"start": v(-29.26, 230.4) * mm, "end": v(-29.26, 233.4) * mm});
            skLineSegment(sketch, "E107", {"start": v(97.74, 233.4) * mm, "end": v(97.74, 230.4) * mm});
            skLineSegment(sketch, "E108", {"start": v(-29.26, 123.4) * mm, "end": v(97.74, 123.14) * mm});
            skLineSegment(sketch, "E109.trimOffspring", {"start": v(97.74, 120.4) * mm, "end": v(109.74, 120.4) * mm});
            skLineSegment(sketch, "E110", {"start": v(-29.26, 230.4) * mm, "end": v(97.74, 230.4) * mm});
            skLineSegment(sketch, "E111.trimOffspring", {"start": v(97.74, 233.4) * mm, "end": v(109.74, 233.4) * mm});
            skLineSegment(sketch, "E112", {"start": v(-41.26, 120.4) * mm, "end": v(-41.26, 154.4) * mm});
            skLineSegment(sketch, "E113", {"start": v(-41.26, 154.4) * mm, "end": v(-44.26, 154.4) * mm});
            skLineSegment(sketch, "E114", {"start": v(-44.26, 199.4) * mm, "end": v(-41.26, 199.4) * mm});
            skLineSegment(sketch, "E115", {"start": v(-41.26, 199.4) * mm, "end": v(-41.26, 233.4) * mm});
            skLineSegment(sketch, "E116", {"start": v(109.74, 233.4) * mm, "end": v(109.74, 199.4) * mm});
            skLineSegment(sketch, "E117", {"start": v(109.74, 199.4) * mm, "end": v(112.74, 199.4) * mm});
            skLineSegment(sketch, "E118", {"start": v(112.74, 154.4) * mm, "end": v(109.74, 154.4) * mm});
            skLineSegment(sketch, "E119", {"start": v(109.74, 154.4) * mm, "end": v(109.74, 120.4) * mm});
            skSolve(sketch);
        }
        {
            var Q0;
            Q0 = qSketchRegion(id + "F12", true);
            extrude(context, id + "F13", {"entities" : qUnion([Q0]), "depth" : 3 * mm});
        }
    });
